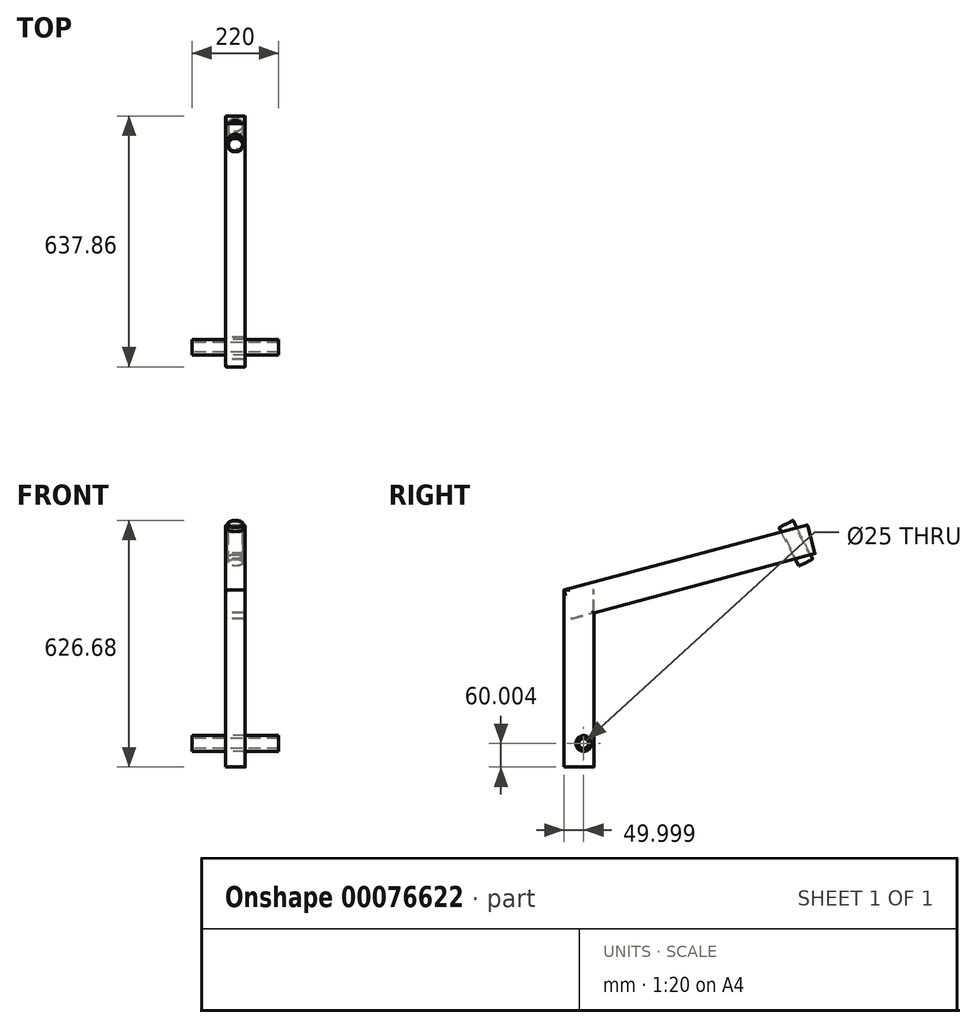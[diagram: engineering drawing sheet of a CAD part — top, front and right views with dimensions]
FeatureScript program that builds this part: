
annotation { "Feature Type Name" : "Feature", "Feature Type Description" : "" }
export const myFeature = defineFeature(function(context is Context, id is Id, definition is map)
    precondition{}
    {
        {
            var Q0;
            Q0=qCreatedBy(makeId("Front.planeOp"),FACE);
            var sketch = newSketch(context, id + "F0", { "sketchPlane" : qUnion([Q0])});
            skLineSegment(sketch, "E0", {"start": v(-104.49, 0) * mm, "end": v(96.85, 0) * mm, "construction": true});
            skSolve(sketch);
        }
        {
            var Q0;
            Q0=sQuery(id+"F0.wireOp",EDGE,"E0");
            var Q1;
            Q1=qCreatedBy(makeId("Front.planeOp"),FACE);
            cPlane(context, id + "F1", {"entities" : qUnion([Q0, Q1]), "cplaneType" : CPlaneType.LINE_ANGLE, "offset" : 25 * mm, "angle" : 15 * degree, "width" : 150 * mm, "height" : 150 * mm});
        }
        {
            assignVariable(context, id + "F2", {"variableType" : VariableType.LENGTH, "name" : "toptubelength", "lengthValue" : 600 * mm});
        }
        {
            assignVariable(context, id + "F3", {"variableType" : VariableType.LENGTH, "name" : "verticaltubelength", "lengthValue" : 450 * mm});
        }
        {
            var Q0;
            Q0=qCreatedBy(id+"F1.planeOp",FACE);
            var sketch = newSketch(context, id + "F4", { "sketchPlane" : qUnion([Q0])});
            skLineSegment(sketch, "E1.bottom", {"start": v(-21, 38) * mm, "end": v(21, 38) * mm});
            skLineSegment(sketch, "E1.top", {"start": v(-21, -38) * mm, "end": v(21, -38) * mm});
            skLineSegment(sketch, "E1.left", {"start": v(-25, 34) * mm, "end": v(-25, -34) * mm});
            skLineSegment(sketch, "E1.right", {"start": v(25, 34) * mm, "end": v(25, -34) * mm});
            skPoint(sketch, "E1.middle", {"position": v(0, 0) * mm});
            skPoint(sketch, "E2.visualSharp", {"position": v(-25, -38) * mm});
            skArc(sketch, "E2.filletArc", {"start": v(-25, -34) * mm, "mid": v(-23.83, -36.83) * mm, "end": v(-21, -38) * mm});
            skPoint(sketch, "E3.visualSharp", {"position": v(25, -38) * mm});
            skArc(sketch, "E3.filletArc", {"start": v(21, -38) * mm, "mid": v(23.83, -36.83) * mm, "end": v(25, -34) * mm});
            skPoint(sketch, "E4.visualSharp", {"position": v(-25, 38) * mm});
            skArc(sketch, "E4.filletArc", {"start": v(-21, 38) * mm, "mid": v(-23.83, 36.83) * mm, "end": v(-25, 34) * mm});
            skPoint(sketch, "E5.visualSharp", {"position": v(25, 38) * mm});
            skArc(sketch, "E5.filletArc", {"start": v(25, 34) * mm, "mid": v(23.83, 36.83) * mm, "end": v(21, 38) * mm});
            skLineSegment(sketch, "E6.0", {"start": v(-23.4, 34) * mm, "end": v(-23.4, -34) * mm});
            skArc(sketch, "E6.1", {"start": v(-21, 36.4) * mm, "mid": v(-22.7, 35.7) * mm, "end": v(-23.4, 34) * mm});
            skArc(sketch, "E6.2", {"start": v(-23.4, -34) * mm, "mid": v(-22.7, -35.7) * mm, "end": v(-21, -36.4) * mm});
            skLineSegment(sketch, "E6.3", {"start": v(-21, 36.4) * mm, "end": v(21, 36.4) * mm});
            skLineSegment(sketch, "E6.4", {"start": v(-21, -36.4) * mm, "end": v(21, -36.4) * mm});
            skArc(sketch, "E6.5", {"start": v(21, -36.4) * mm, "mid": v(22.7, -35.7) * mm, "end": v(23.4, -34) * mm});
            skLineSegment(sketch, "E6.6", {"start": v(23.4, 34) * mm, "end": v(23.4, -34) * mm});
            skArc(sketch, "E6.7", {"start": v(23.4, 34) * mm, "mid": v(22.7, 35.7) * mm, "end": v(21, 36.4) * mm});
            skSolve(sketch);
        }
        {
            var Q0;
            Q0=makeQuery(id+"F4.imprint","IMPRINT",FACE,{"disambiguationData":[TD([[makeQuery(id+"F4.imprint","IMPRINT",EDGE,{"derivedFrom":sQuery(id+"F4.wireOp",EDGE,"E1.bottom")}),-1.0]])]});
            extrude(context, id + "F5", {"entities" : qUnion([Q0]), "flatOperationType" : FlatOperationType.REMOVE, "oppositeDirection" : true, "depth" : getVariable(context, 'toptubelength'), "offsetDistance" : 25 * mm, "domain" : OperationDomain.MODEL});
        }
        {
            var Q0;
            Q0=makeQuery(id+"F5.opExtrude","CAP_EDGE",EDGE,{"disambiguationData":[OSD([sQuery(id+"F4.wireOp",EDGE,"E1.bottom")])],"isStart":false});
            cPlane(context, id + "F6", {"entities" : qUnion([Q0]), "cplaneType" : CPlaneType.LINE_ANGLE, "offset" : 25 * mm, "angle" : 90 * degree, "width" : 150 * mm, "height" : 150 * mm});
        }
        {
            var Q0;
            Q0=qCreatedBy(id+"F6.planeOp",FACE);
            var sketch = newSketch(context, id + "F7", { "sketchPlane" : qUnion([Q0])});
            skLineSegment(sketch, "E7.bottom", {"start": v(-21, -589.4) * mm, "end": v(21, -589.4) * mm});
            skLineSegment(sketch, "E7.top", {"start": v(-21, -513.4) * mm, "end": v(21, -513.4) * mm});
            skLineSegment(sketch, "E7.left", {"start": v(-25, -585.4) * mm, "end": v(-25, -517.4) * mm});
            skLineSegment(sketch, "E7.right", {"start": v(25, -585.4) * mm, "end": v(25, -517.4) * mm});
            skPoint(sketch, "E8.visualSharp", {"position": v(-25, -589.4) * mm});
            skArc(sketch, "E8.filletArc", {"start": v(-25, -585.4) * mm, "mid": v(-23.83, -588.22) * mm, "end": v(-21, -589.4) * mm});
            skPoint(sketch, "E9.visualSharp", {"position": v(25, -589.4) * mm});
            skArc(sketch, "E9.filletArc", {"start": v(21, -589.4) * mm, "mid": v(23.83, -588.22) * mm, "end": v(25, -585.4) * mm});
            skPoint(sketch, "E10.visualSharp", {"position": v(25, -513.4) * mm});
            skArc(sketch, "E10.filletArc", {"start": v(25, -517.4) * mm, "mid": v(23.83, -514.56) * mm, "end": v(21, -513.4) * mm});
            skPoint(sketch, "E11.visualSharp", {"position": v(-25, -513.4) * mm});
            skArc(sketch, "E11.filletArc", {"start": v(-21, -513.4) * mm, "mid": v(-23.83, -514.56) * mm, "end": v(-25, -517.4) * mm});
            skArc(sketch, "E12.0", {"start": v(-23.4, -585.4) * mm, "mid": v(-22.7, -587.09) * mm, "end": v(-21, -587.8) * mm});
            skLineSegment(sketch, "E12.1", {"start": v(-23.4, -585.4) * mm, "end": v(-23.4, -517.4) * mm});
            skLineSegment(sketch, "E12.2", {"start": v(-21, -587.8) * mm, "end": v(21, -587.8) * mm});
            skArc(sketch, "E12.3", {"start": v(-21, -515) * mm, "mid": v(-22.7, -515.7) * mm, "end": v(-23.4, -517.4) * mm});
            skArc(sketch, "E12.4", {"start": v(21, -587.8) * mm, "mid": v(22.7, -587.09) * mm, "end": v(23.4, -585.4) * mm});
            skLineSegment(sketch, "E12.5", {"start": v(23.4, -585.4) * mm, "end": v(23.4, -517.4) * mm});
            skArc(sketch, "E12.6", {"start": v(23.4, -517.4) * mm, "mid": v(22.7, -515.7) * mm, "end": v(21, -515) * mm});
            skLineSegment(sketch, "E12.7", {"start": v(-21, -515) * mm, "end": v(21, -515) * mm});
            skSolve(sketch);
        }
        {
            var Q0;
            Q0 = qSketchRegion(id + "F7", true);
            var Q1;
            Q1 = qConstructionFilter(qBodyType(qCreatedBy(id + "F7" ,EDGE), BodyType.WIRE), ConstructionObject.NO);
            extrude(context, id + "F8", {"entities" : qUnion([Q0]), "operationType" : NewBodyOperationType.ADD, "flatOperationType" : FlatOperationType.REMOVE, "surfaceEntities" : qUnion([Q1]), "oppositeDirection" : true, "depth" : getVariable(context, 'verticaltubelength'), "offsetDistance" : 25 * mm, "domain" : OperationDomain.MODEL});
        }
        {
            var Q0;
            Q0=makeQuery(id+"F5.opExtrude","CAP_FACE",FACE,{"disambiguationData":[OSD([sQuery(id+"F4.wireOp",EDGE,"E1.bottom"),sQuery(id+"F4.wireOp",EDGE,"E1.top"),sQuery(id+"F4.wireOp",EDGE,"E1.left"),sQuery(id+"F4.wireOp",EDGE,"E1.right"),sQuery(id+"F4.wireOp",EDGE,"E2.filletArc"),sQuery(id+"F4.wireOp",EDGE,"E3.filletArc"),sQuery(id+"F4.wireOp",EDGE,"E4.filletArc"),sQuery(id+"F4.wireOp",EDGE,"E5.filletArc"),sQuery(id+"F4.wireOp",EDGE,"E6.0"),sQuery(id+"F4.wireOp",EDGE,"E6.1"),sQuery(id+"F4.wireOp",EDGE,"E6.2"),sQuery(id+"F4.wireOp",EDGE,"E6.3"),sQuery(id+"F4.wireOp",EDGE,"E6.4"),sQuery(id+"F4.wireOp",EDGE,"E6.5"),sQuery(id+"F4.wireOp",EDGE,"E6.6"),sQuery(id+"F4.wireOp",EDGE,"E6.7")])],"isStart":true});
            extrude(context, id + "F9", {"entities" : qUnion([Q0]), "operationType" : NewBodyOperationType.ADD, "depth" : 40 * mm, "offsetDistance" : 25 * mm});
        }
        {
            var Q0;
            Q0=sQuery(id+"F0.wireOp",EDGE,"E0");
            var Q1;
            Q1=qCreatedBy(makeId("Top.planeOp"),FACE);
            cPlane(context, id + "F10", {"entities" : qUnion([Q0, Q1]), "cplaneType" : CPlaneType.LINE_ANGLE, "offset" : 25 * mm, "angle" : 27 * degree, "width" : 150 * mm, "height" : 150 * mm});
        }
        {
            var Q0;
            Q0=qCreatedBy(id+"F10.planeOp",FACE);
            var sketch = newSketch(context, id + "F11", { "sketchPlane" : qUnion([Q0])});
            skCircle(sketch, "E13", {"center": v(0, 0) * mm, "radius": 20 * mm});
            skCircle(sketch, "E14", {"center": v(0, 0) * mm, "radius": 18 * mm});
            skSolve(sketch);
        }
        {
            var Q0;
            {var subQ0=sQuery(id+"F4.wireOp",EDGE,"E1.left");Q0=makeQuery(id+"F9.boolean.opBoolean","MERGE",FACE,{"derivedFrom":[makeQuery(id+"F8.boolean.opBoolean","MERGE",FACE,{"derivedFrom":[makeQuery(id+"F5.opExtrude","SWEPT_FACE",FACE,{"disambiguationData":[OSD([subQ0])]}),makeQuery(id+"F8.opExtrude","SWEPT_FACE",FACE,{"disambiguationData":[OSD([sQuery(id+"F7.wireOp",EDGE,"E7.right")])]})]}),makeQuery(id+"F9.opExtrude","SWEPT_FACE",FACE,{"disambiguationData":[OSD([subQ0])]})]});}
            var sketch = newSketch(context, id + "F12", { "sketchPlane" : qUnion([Q0])});
            skCircle(sketch, "E15", {"center": v(-539.4, -508.59) * mm, "radius": 20 * mm});
            skPoint(sketch, "E15.centerSnap0", {"position": v(-539.4, -568.59) * mm});
            skSolve(sketch);
        }
        {
            var Q0;
            Q0 = qSketchRegion(id + "F12", true);
            extrude(context, id + "F13", {"entities" : qUnion([Q0]), "operationType" : NewBodyOperationType.REMOVE, "endBound" : BoundingType.THROUGH_ALL, "oppositeDirection" : true, "depth" : 25 * mm, "offsetDistance" : 25 * mm});
        }
        {
            var Q0;
            Q0=qCreatedBy(makeId("Right.planeOp"),FACE);
            var sketch = newSketch(context, id + "F14", { "sketchPlane" : qUnion([Q0])});
            skCircle(sketch, "E16", {"center": v(-539.4, -508.59) * mm, "radius": 20 * mm});
            skCircle(sketch, "E17", {"center": v(-539.4, -508.59) * mm, "radius": 12.5 * mm});
            skSolve(sketch);
        }
        {
            var Q0;
            Q0 = qSketchRegion(id + "F14", true);
            extrude(context, id + "F15", {"entities" : qUnion([Q0]), "operationType" : NewBodyOperationType.ADD, "flatOperationType" : FlatOperationType.REMOVE, "endBound" : BoundingType.SYMMETRIC, "depth" : 100 * mm, "offsetDistance" : 25 * mm, "domain" : OperationDomain.MODEL});
        }
        {
            var Q0;
            Q0=makeQuery(id+"F11.imprint","IMPRINT",FACE,{"disambiguationData":[TD([[makeQuery(id+"F11.imprint","IMPRINT",EDGE,{"derivedFrom":sQuery(id+"F11.wireOp",EDGE,"E14")}),1.0]])]});
            var Q1;
            Q1=makeQuery(id+"F11.imprint","IMPRINT",FACE,{"disambiguationData":[TD([[makeQuery(id+"F11.imprint","IMPRINT",EDGE,{"derivedFrom":sQuery(id+"F11.wireOp",EDGE,"E13")}),1.0]])]});
            extrude(context, id + "F16", {"entities" : qUnion([Q0, Q1]), "operationType" : NewBodyOperationType.REMOVE, "endBound" : BoundingType.SYMMETRIC, "oppositeDirection" : true, "depth" : 113.8 * mm, "offsetDistance" : 25 * mm});
        }
        {
            var Q0;
            Q0=makeQuery(id+"F11.imprint","IMPRINT",FACE,{"disambiguationData":[TD([[makeQuery(id+"F11.imprint","IMPRINT",EDGE,{"derivedFrom":sQuery(id+"F11.wireOp",EDGE,"E13")}),1.0]])]});
            extrude(context, id + "F17", {"entities" : qUnion([Q0]), "operationType" : NewBodyOperationType.ADD, "endBound" : BoundingType.SYMMETRIC, "depth" : 110 * mm, "offsetDistance" : 25 * mm});
        }
        {
            var Q0;
            Q0=makeQuery(id+"F9.opExtrude","CAP_FACE",FACE,{"disambiguationData":[OSD([sQuery(id+"F4.wireOp",EDGE,"E1.bottom"),sQuery(id+"F4.wireOp",EDGE,"E1.top"),sQuery(id+"F4.wireOp",EDGE,"E1.left"),sQuery(id+"F4.wireOp",EDGE,"E1.right"),sQuery(id+"F4.wireOp",EDGE,"E2.filletArc"),sQuery(id+"F4.wireOp",EDGE,"E3.filletArc"),sQuery(id+"F4.wireOp",EDGE,"E4.filletArc"),sQuery(id+"F4.wireOp",EDGE,"E5.filletArc"),sQuery(id+"F4.wireOp",EDGE,"E6.0"),sQuery(id+"F4.wireOp",EDGE,"E6.1"),sQuery(id+"F4.wireOp",EDGE,"E6.2"),sQuery(id+"F4.wireOp",EDGE,"E6.3"),sQuery(id+"F4.wireOp",EDGE,"E6.4"),sQuery(id+"F4.wireOp",EDGE,"E6.5"),sQuery(id+"F4.wireOp",EDGE,"E6.6"),sQuery(id+"F4.wireOp",EDGE,"E6.7")])],"isStart":false});
            var sketch = newSketch(context, id + "F18", { "sketchPlane" : qUnion([Q0])});
            skLineSegment(sketch, "E18.0", {"start": v(-25, 34) * mm, "end": v(-25, -34) * mm});
            skArc(sketch, "E19.0", {"start": v(-21, 38) * mm, "mid": v(-23.83, 36.83) * mm, "end": v(-25, 34) * mm});
            skLineSegment(sketch, "E20.0", {"start": v(-21, 38) * mm, "end": v(21, 38) * mm});
            skArc(sketch, "E21.0", {"start": v(25, 34) * mm, "mid": v(23.83, 36.83) * mm, "end": v(21, 38) * mm});
            skLineSegment(sketch, "E22.0", {"start": v(25, 34) * mm, "end": v(25, -34) * mm});
            skArc(sketch, "E23.0", {"start": v(21, -38) * mm, "mid": v(23.83, -36.83) * mm, "end": v(25, -34) * mm});
            skLineSegment(sketch, "E24.0", {"start": v(-21, -38) * mm, "end": v(21, -38) * mm});
            skArc(sketch, "E25.0", {"start": v(-25, -34) * mm, "mid": v(-23.83, -36.83) * mm, "end": v(-21, -38) * mm});
            skLineSegment(sketch, "E26.0.4", {"start": v(25, -34) * mm, "end": v(25, 34) * mm});
            skLineSegment(sketch, "E26.0.6", {"start": v(21, 38) * mm, "end": v(-21, 38) * mm});
            skSolve(sketch);
        }
        {
            var Q0;
            Q0=makeQuery(id+"F15.opExtrude","CAP_FACE",FACE,{"disambiguationData":[OSD([sQuery(id+"F14.wireOp",EDGE,"E16"),sQuery(id+"F14.wireOp",EDGE,"E17")])],"isStart":false});
            var sketch = newSketch(context, id + "F19", { "sketchPlane" : qUnion([Q0])});
            skCircle(sketch, "E27.0", {"center": v(-539.4, -508.59) * mm, "radius": 20 * mm});
            skCircle(sketch, "E28.0", {"center": v(-539.4, -508.59) * mm, "radius": 12.5 * mm});
            skSolve(sketch);
        }
        {
            var Q0;
            Q0=makeQuery(id+"F19.imprint","IMPRINT",FACE,{"disambiguationData":[TD([[makeQuery(id+"F19.imprint","IMPRINT",EDGE,{"derivedFrom":sQuery(id+"F19.wireOp",EDGE,"E27.0")}),1.0]])]});
            extrude(context, id + "F20", {"entities" : qUnion([Q0]), "flatOperationType" : FlatOperationType.REMOVE, "depth" : 60 * mm, "offsetDistance" : 25 * mm, "domain" : OperationDomain.MODEL});
        }
        {
            var Q0;
            Q0=makeQuery(id+"FgPjlfOF3R3v0L9_3.opExtrude","SWEPT_BODY",BODY,{"disambiguationData":[OSD([sQuery(id+"F7JuR7eFcYRdl6T_3.wireOp",EDGE,"6547265c-1e15-4a6a-8d82-62e7825cdf54.filletArc")])]});
            var Q1;
            Q1=makeQuery(id+"F20.opExtrude","SWEPT_BODY",BODY,{"disambiguationData":[OSD([sQuery(id+"F19.wireOp",EDGE,"E27.0"),sQuery(id+"F19.wireOp",EDGE,"E28.0")])]});
            var Q2;
            Q2=qCreatedBy(makeId("Right.planeOp"),FACE);
            mirror(context, id + "F21", {"operationType" : NewBodyOperationType.ADD, "entities" : qUnion([Q0, Q1]), "mirrorPlane" : qUnion([Q2])});
        }
    });
